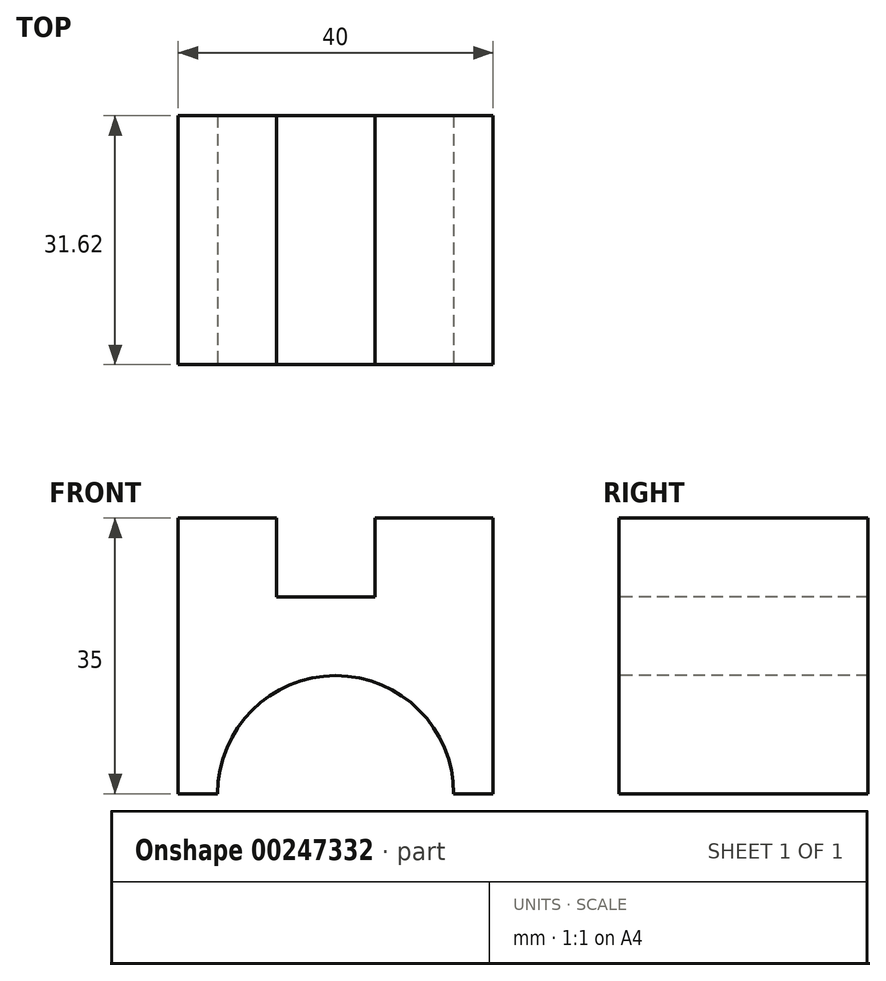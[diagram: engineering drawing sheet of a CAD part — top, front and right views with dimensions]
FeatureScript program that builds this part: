
annotation { "Feature Type Name" : "Feature", "Feature Type Description" : "" }
export const myFeature = defineFeature(function(context is Context, id is Id, definition is map)
    precondition{}
    {
        {
            var Q0;
            Q0=qCreatedBy(makeId("Top.planeOp"),FACE);
            var sketch = newSketch(context, id + "F0", { "sketchPlane" : qUnion([Q0])});
            skLineSegment(sketch, "E0", {"start": v(0, 0) * mm, "end": v(40, 0) * mm});
            skLineSegment(sketch, "E1", {"start": v(40, 0) * mm, "end": v(40, -31.62) * mm});
            skLineSegment(sketch, "E2", {"start": v(40, -31.62) * mm, "end": v(0, -31.62) * mm});
            skLineSegment(sketch, "E3", {"start": v(0, -31.62) * mm, "end": v(0, 0) * mm});
            skSolve(sketch);
        }
        {
            var Q0;
            Q0 = qSketchRegion(id + "F0", true);
            extrude(context, id + "F1", {"entities" : qUnion([Q0]), "depth" : 35 * mm});
        }
        {
            var Q0;
            Q0=makeQuery(id+"F1.opExtrude","CAP_FACE",FACE,{"disambiguationData":[OSD([sQuery(id+"F0.wireOp",EDGE,"E0"),sQuery(id+"F0.wireOp",EDGE,"E1"),sQuery(id+"F0.wireOp",EDGE,"E2"),sQuery(id+"F0.wireOp",EDGE,"E3")])],"isStart":false});
            var sketch = newSketch(context, id + "F2", { "sketchPlane" : qUnion([Q0])});
            skLineSegment(sketch, "E4", {"start": v(40, -18.62) * mm, "end": v(25, -18.62) * mm});
            skLineSegment(sketch, "E5", {"start": v(25, -18.62) * mm, "end": v(25, 0) * mm});
            skLineSegment(sketch, "E6", {"start": v(25, -18.62) * mm, "end": v(25, -31.62) * mm});
            skLineSegment(sketch, "E7", {"start": v(0, -18.33) * mm, "end": v(12.5, -18.33) * mm});
            skLineSegment(sketch, "E8", {"start": v(12.5, -18.33) * mm, "end": v(12.5, 0) * mm});
            skLineSegment(sketch, "E9", {"start": v(12.5, -18.33) * mm, "end": v(12.5, -31.62) * mm});
            skSolve(sketch);
        }
        {
            var Q0;
            Q0 = qSketchRegion(id + "F2", true);
            var Q1;
            {var subQ3=sQuery(id+"F2.wireOp",EDGE,"E5");Q1=makeQuery(id+"F2.imprint","IMPRINT",FACE,{"disambiguationData":[TD([[makeQuery(id+"F2.imprint","IMPRINT",EDGE,{"derivedFrom":subQ3}),1.0]])]});}
            extrude(context, id + "F3", {"entities" : qUnion([Q0, Q1]), "operationType" : NewBodyOperationType.REMOVE, "oppositeDirection" : true, "depth" : 10 * mm});
        }
        {
            var Q0;
            Q0=makeQuery(id+"F1.opExtrude","SWEPT_FACE",FACE,{"disambiguationData":[OSD([sQuery(id+"F0.wireOp",EDGE,"E2")])]});
            var sketch = newSketch(context, id + "F4", { "sketchPlane" : qUnion([Q0])});
            skArc(sketch, "E10", {"start": v(35, 0) * mm, "mid": v(20, 15) * mm, "end": v(5, 0) * mm});
            skLineSegment(sketch, "E11.0", {"start": v(35, 0) * mm, "end": v(5, 0) * mm});
            skPoint(sketch, "E12.orphan", {"position": v(40, 0) * mm});
            skPoint(sketch, "E13.orphan", {"position": v(0, 0) * mm});
            skSolve(sketch);
        }
        {
            var Q0;
            Q0=makeQuery(id+"F4.imprint","IMPRINT",FACE,{"disambiguationData":[TD([[makeQuery(id+"F4.imprint","IMPRINT",EDGE,{"derivedFrom":sQuery(id+"F4.wireOp",EDGE,"E10")}),1.0]])]});
            extrude(context, id + "F5", {"entities" : qUnion([Q0]), "operationType" : NewBodyOperationType.REMOVE, "oppositeDirection" : true, "depth" : 40 * mm});
        }
    });
